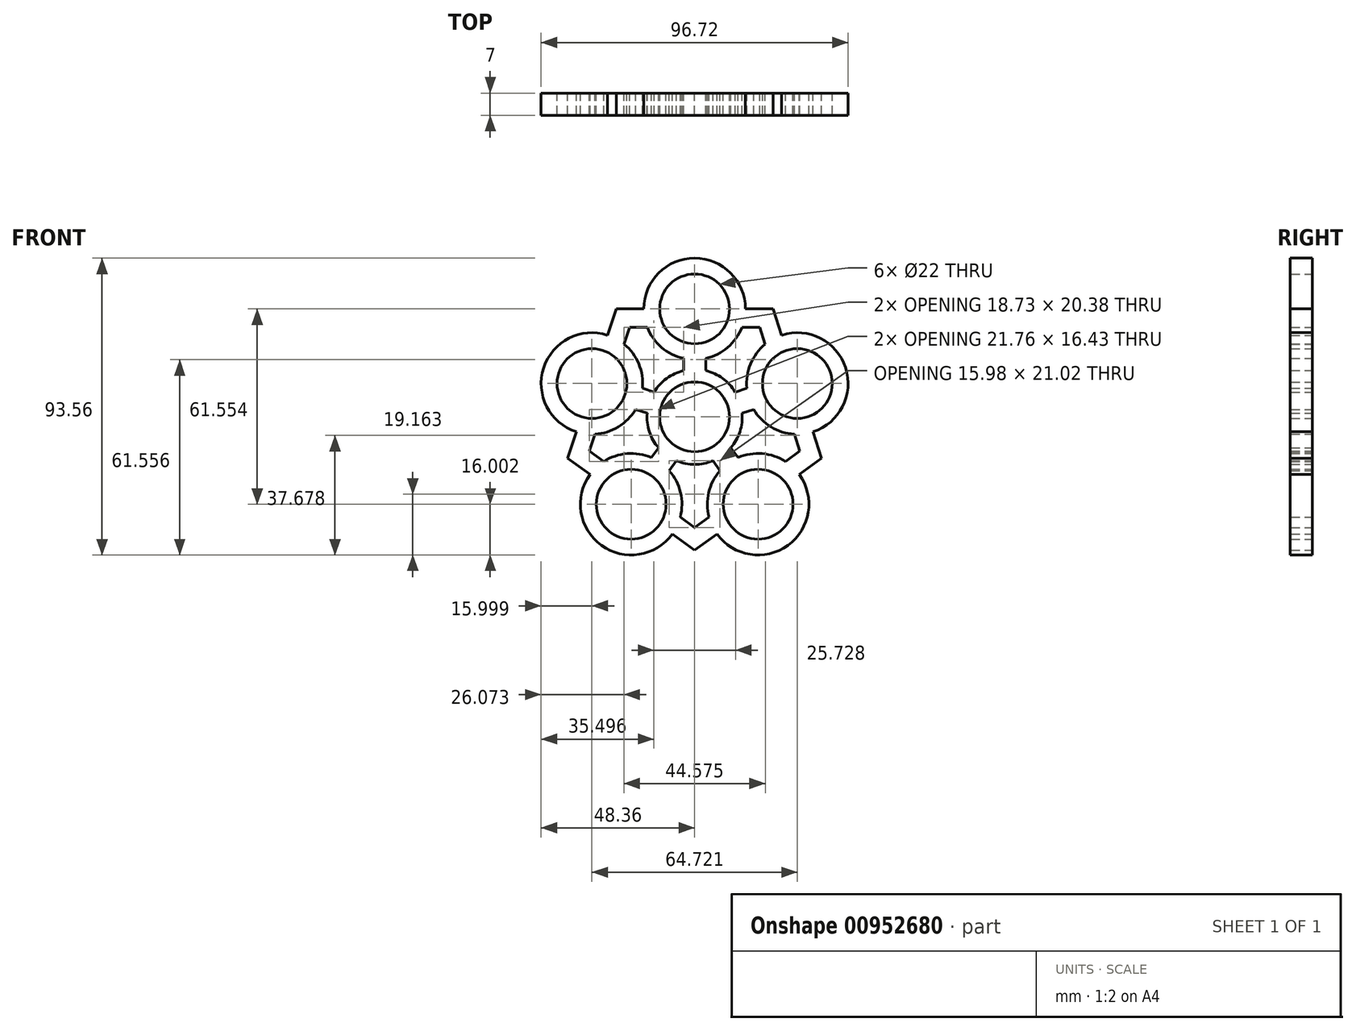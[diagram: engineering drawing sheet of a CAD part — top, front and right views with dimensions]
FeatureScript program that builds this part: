
annotation { "Feature Type Name" : "Feature", "Feature Type Description" : "" }
export const myFeature = defineFeature(function(context is Context, id is Id, definition is map)
    precondition{}
    {
        {
            var Q0;
            Q0=qCreatedBy(makeId("Front.planeOp"),FACE);
            var sketch = newSketch(context, id + "F0", { "sketchPlane" : qUnion([Q0])});
            skCircle(sketch, "E0", {"center": v(0, 0) * mm, "radius": 11 * mm});
            skCircle(sketch, "E1", {"center": v(0, 0) * mm, "radius": 15 * mm});
            skPoint(sketch, "E2.0.midPoint", {"position": v(0, -27.53) * mm});
            skCircle(sketch, "E3", {"center": v(0, 34.03) * mm, "radius": 11 * mm});
            skCircle(sketch, "E4", {"center": v(0, 34.03) * mm, "radius": 16 * mm});
            skCircle(sketch, "E5", {"center": v(32.36, 10.51) * mm, "radius": 11 * mm});
            skCircle(sketch, "E6", {"center": v(32.36, 10.51) * mm, "radius": 16 * mm});
            skCircle(sketch, "E7", {"center": v(20, -27.53) * mm, "radius": 11 * mm});
            skCircle(sketch, "E8", {"center": v(20, -27.53) * mm, "radius": 16 * mm});
            skCircle(sketch, "E9", {"center": v(-20, -27.53) * mm, "radius": 11 * mm});
            skCircle(sketch, "E10", {"center": v(-20, -27.53) * mm, "radius": 16 * mm});
            skCircle(sketch, "E11", {"center": v(-32.36, 10.51) * mm, "radius": 11 * mm});
            skCircle(sketch, "E12", {"center": v(-32.36, 10.51) * mm, "radius": 16 * mm});
            skPoint(sketch, "E13.0.midPoint", {"position": v(0, 28.22) * mm});
            skLineSegment(sketch, "E14.0", {"start": v(-24.72, 34.03) * mm, "end": v(-11, 34.03) * mm});
            skLineSegment(sketch, "E14.1", {"start": v(24.72, 34.03) * mm, "end": v(28.96, 20.98) * mm});
            skLineSegment(sketch, "E14.2", {"start": v(40, -13) * mm, "end": v(32.94, -18.12) * mm});
            skLineSegment(sketch, "E14.3", {"start": v(0, -42.06) * mm, "end": v(-11.1, -34) * mm});
            skLineSegment(sketch, "E14.4", {"start": v(-40, -13) * mm, "end": v(-35.76, 0.05) * mm});
            skLineSegment(sketch, "E15.trimOffspring", {"start": v(11, 34.03) * mm, "end": v(24.72, 34.03) * mm});
            skLineSegment(sketch, "E16.trimOffspring", {"start": v(7.06, -36.93) * mm, "end": v(0, -42.06) * mm});
            skLineSegment(sketch, "E17.trimOffspring", {"start": v(35.76, 0.05) * mm, "end": v(40, -13) * mm});
            skLineSegment(sketch, "E18.trimOffspring", {"start": v(-28.9, -21.06) * mm, "end": v(-40, -13) * mm});
            skLineSegment(sketch, "E19.trimOffspring", {"start": v(-28.96, 20.98) * mm, "end": v(-24.72, 34.03) * mm});
            skCircle(sketch, "E20.cCircle", {"center": v(0, 0) * mm, "radius": 28.22 * mm, "construction": true});
            skLineSegment(sketch, "E20.0", {"start": v(-20.5, 28.22) * mm, "end": v(20.5, 28.22) * mm});
            skLineSegment(sketch, "E20.1", {"start": v(20.5, 28.22) * mm, "end": v(33.17, -10.78) * mm});
            skLineSegment(sketch, "E20.2", {"start": v(33.17, -10.78) * mm, "end": v(0, -34.88) * mm});
            skLineSegment(sketch, "E20.3", {"start": v(0, -34.88) * mm, "end": v(-33.17, -10.78) * mm});
            skLineSegment(sketch, "E20.4", {"start": v(-33.17, -10.78) * mm, "end": v(-20.5, 28.22) * mm});
            skLineSegment(sketch, "E21", {"start": v(32.94, -18.12) * mm, "end": v(7.06, -36.93) * mm});
            skLineSegment(sketch, "E22", {"start": v(-11.1, -34) * mm, "end": v(-28.9, -21.06) * mm});
            skLineSegment(sketch, "E23", {"start": v(-35.76, 0.05) * mm, "end": v(-28.96, 20.98) * mm});
            skLineSegment(sketch, "E24", {"start": v(-11, 34.03) * mm, "end": v(11, 34.03) * mm});
            skLineSegment(sketch, "E25", {"start": v(28.96, 20.98) * mm, "end": v(35.76, 0.05) * mm});
            skCircle(sketch, "E26.cCircle", {"center": v(0, 0) * mm, "radius": 4.82 * mm, "construction": true});
            skLineSegment(sketch, "E26.0", {"start": v(-3.5, 4.82) * mm, "end": v(3.5, 4.82) * mm});
            skLineSegment(sketch, "E26.1", {"start": v(3.5, 4.82) * mm, "end": v(5.66, -1.84) * mm});
            skLineSegment(sketch, "E26.2", {"start": v(5.66, -1.84) * mm, "end": v(0, -5.95) * mm});
            skLineSegment(sketch, "E26.3", {"start": v(0, -5.95) * mm, "end": v(-5.66, -1.84) * mm});
            skLineSegment(sketch, "E26.4", {"start": v(-5.66, -1.84) * mm, "end": v(-3.5, 4.82) * mm});
            skPoint(sketch, "E26.0.midPoint", {"position": v(0, 4.82) * mm});
            skLineSegment(sketch, "E27", {"start": v(3.5, 4.82) * mm, "end": v(31.28, 13.84) * mm});
            skLineSegment(sketch, "E28", {"start": v(5.66, -1.84) * mm, "end": v(33.44, 7.19) * mm});
            skLineSegment(sketch, "E29", {"start": v(5.66, -1.84) * mm, "end": v(19.29, -20.6) * mm});
            skLineSegment(sketch, "E30", {"start": v(0, -5.95) * mm, "end": v(13.63, -24.7) * mm});
            skLineSegment(sketch, "E31", {"start": v(0, -5.95) * mm, "end": v(-13.63, -24.7) * mm});
            skLineSegment(sketch, "E32", {"start": v(-5.66, -1.84) * mm, "end": v(-19.29, -20.6) * mm});
            skLineSegment(sketch, "E33", {"start": v(-5.66, -1.84) * mm, "end": v(-27.7, 5.32) * mm});
            skLineSegment(sketch, "E34", {"start": v(-3.5, 4.82) * mm, "end": v(-25.55, 11.98) * mm});
            skLineSegment(sketch, "E35", {"start": v(-3.5, 4.82) * mm, "end": v(-3.5, 28) * mm});
            skLineSegment(sketch, "E36", {"start": v(3.5, 4.82) * mm, "end": v(3.5, 28) * mm});
            skSolve(sketch);
        }
        {
            var Q0;
            {var subQ1=sQuery(id+"F0.wireOp",EDGE,"E14.1");var subQ6=sQuery(id+"F0.wireOp",EDGE,"E6");var subQ8=makeQuery(id+"F0.imprint","INTERSECT",VERTEX,{"derivedFrom":[subQ6,subQ1]});Q0=makeQuery(id+"F0.imprint","IMPRINT",FACE,{"disambiguationData":[TD([[makeQuery(id+"F0.imprint","IMPRINT",EDGE,{"disambiguationData":[TD([[subQ8,1.0]])],"derivedFrom":subQ6}),1.0]])]});}
            var Q1;
            {var subQ0=sQuery(id+"F0.wireOp",EDGE,"E14.1");var subQ5=sQuery(id+"F0.wireOp",EDGE,"E6");var subQ6=makeQuery(id+"F0.imprint","INTERSECT",VERTEX,{"derivedFrom":[subQ5,subQ0]});Q1=makeQuery(id+"F0.imprint","IMPRINT",FACE,{"disambiguationData":[TD([[makeQuery(id+"F0.imprint","IMPRINT",EDGE,{"disambiguationData":[TD([[subQ6,-1.0]])],"derivedFrom":subQ5}),1.0]])]});}
            var Q2;
            {var subQ0=sQuery(id+"F0.wireOp",EDGE,"E20.1");var subQ1=sQuery(id+"F0.wireOp",EDGE,"E5");var subQ2=makeQuery(id+"F0.imprint","INTERSECT",VERTEX,{"disambiguationData":[OD(0.0)],"derivedFrom":[subQ1,subQ0]});Q2=makeQuery(id+"F0.imprint","IMPRINT",FACE,{"disambiguationData":[TD([[makeQuery(id+"F0.imprint","IMPRINT",EDGE,{"disambiguationData":[TD([[subQ2,-1.0]])],"derivedFrom":subQ1}),-1.0]])]});}
            var Q3;
            {var subQ0=sQuery(id+"F0.wireOp",EDGE,"E27");var subQ1=sQuery(id+"F0.wireOp",EDGE,"E5");var subQ2=makeQuery(id+"F0.imprint","INTERSECT",VERTEX,{"derivedFrom":[subQ1,subQ0]});Q3=makeQuery(id+"F0.imprint","IMPRINT",FACE,{"disambiguationData":[TD([[makeQuery(id+"F0.imprint","IMPRINT",EDGE,{"disambiguationData":[TD([[subQ2,-1.0]])],"derivedFrom":subQ1}),-1.0]])]});}
            var Q4;
            {var subQ0=sQuery(id+"F0.wireOp",EDGE,"E17.trimOffspring");var subQ5=sQuery(id+"F0.wireOp",EDGE,"E6");var subQ6=makeQuery(id+"F0.imprint","INTERSECT",VERTEX,{"derivedFrom":[subQ5,subQ0]});Q4=makeQuery(id+"F0.imprint","IMPRINT",FACE,{"disambiguationData":[TD([[makeQuery(id+"F0.imprint","IMPRINT",EDGE,{"disambiguationData":[TD([[subQ6,1.0]])],"derivedFrom":subQ5}),1.0]])]});}
            var Q5;
            {var subQ0=sQuery(id+"F0.wireOp",EDGE,"E28");var subQ1=sQuery(id+"F0.wireOp",EDGE,"E5");var subQ2=makeQuery(id+"F0.imprint","INTERSECT",VERTEX,{"derivedFrom":[subQ1,subQ0]});Q5=makeQuery(id+"F0.imprint","IMPRINT",FACE,{"disambiguationData":[TD([[makeQuery(id+"F0.imprint","IMPRINT",EDGE,{"disambiguationData":[TD([[subQ2,-1.0]])],"derivedFrom":subQ1}),-1.0]])]});}
            var Q6;
            {var subQ1=sQuery(id+"F0.wireOp",EDGE,"E14.2");Q6=makeQuery(id+"F0.imprint","IMPRINT",FACE,{"disambiguationData":[TD([[makeQuery(id+"F0.imprint","IMPRINT",EDGE,{"derivedFrom":subQ1}),-1.0]])]});}
            var Q7;
            {var subQ0=sQuery(id+"F0.wireOp",EDGE,"E21");var subQ1=sQuery(id+"F0.wireOp",EDGE,"E7");var subQ2=makeQuery(id+"F0.imprint","INTERSECT",VERTEX,{"disambiguationData":[OD(0.0)],"derivedFrom":[subQ1,subQ0]});Q7=makeQuery(id+"F0.imprint","IMPRINT",FACE,{"disambiguationData":[TD([[makeQuery(id+"F0.imprint","IMPRINT",EDGE,{"disambiguationData":[TD([[subQ2,1.0]])],"derivedFrom":subQ1}),-1.0]])]});}
            var Q8;
            {var subQ0=sQuery(id+"F0.wireOp",EDGE,"E20.2");var subQ1=sQuery(id+"F0.wireOp",EDGE,"E7");var subQ2=makeQuery(id+"F0.imprint","INTERSECT",VERTEX,{"disambiguationData":[OD(0.0)],"derivedFrom":[subQ1,subQ0]});Q8=makeQuery(id+"F0.imprint","IMPRINT",FACE,{"disambiguationData":[TD([[makeQuery(id+"F0.imprint","IMPRINT",EDGE,{"disambiguationData":[TD([[subQ2,1.0]])],"derivedFrom":subQ1}),-1.0]])]});}
            var Q9;
            {var subQ0=sQuery(id+"F0.wireOp",EDGE,"E29");var subQ1=sQuery(id+"F0.wireOp",EDGE,"E7");var subQ2=makeQuery(id+"F0.imprint","INTERSECT",VERTEX,{"derivedFrom":[subQ1,subQ0]});Q9=makeQuery(id+"F0.imprint","IMPRINT",FACE,{"disambiguationData":[TD([[makeQuery(id+"F0.imprint","IMPRINT",EDGE,{"disambiguationData":[TD([[subQ2,1.0]])],"derivedFrom":subQ1}),-1.0]])]});}
            var Q10;
            {var subQ0=sQuery(id+"F0.wireOp",EDGE,"E29");var subQ1=sQuery(id+"F0.wireOp",EDGE,"E7");var subQ2=makeQuery(id+"F0.imprint","INTERSECT",VERTEX,{"derivedFrom":[subQ1,subQ0]});Q10=makeQuery(id+"F0.imprint","IMPRINT",FACE,{"disambiguationData":[TD([[makeQuery(id+"F0.imprint","IMPRINT",EDGE,{"disambiguationData":[TD([[subQ2,-1.0]])],"derivedFrom":subQ1}),-1.0]])]});}
            var Q11;
            {var subQ0=sQuery(id+"F0.wireOp",EDGE,"E30");var subQ1=sQuery(id+"F0.wireOp",EDGE,"E7");var subQ2=makeQuery(id+"F0.imprint","INTERSECT",VERTEX,{"derivedFrom":[subQ1,subQ0]});Q11=makeQuery(id+"F0.imprint","IMPRINT",FACE,{"disambiguationData":[TD([[makeQuery(id+"F0.imprint","IMPRINT",EDGE,{"disambiguationData":[TD([[subQ2,-1.0]])],"derivedFrom":subQ1}),-1.0]])]});}
            var Q12;
            {var subQ0=sQuery(id+"F0.wireOp",EDGE,"E20.2");var subQ1=sQuery(id+"F0.wireOp",EDGE,"E7");var subQ2=makeQuery(id+"F0.imprint","INTERSECT",VERTEX,{"disambiguationData":[OD(1.0)],"derivedFrom":[subQ1,subQ0]});Q12=makeQuery(id+"F0.imprint","IMPRINT",FACE,{"disambiguationData":[TD([[makeQuery(id+"F0.imprint","IMPRINT",EDGE,{"disambiguationData":[TD([[subQ2,-1.0]])],"derivedFrom":subQ1}),-1.0]])]});}
            var Q13;
            {var subQ0=sQuery(id+"F0.wireOp",EDGE,"E14.3");var subQ5=sQuery(id+"F0.wireOp",EDGE,"E10");var subQ6=makeQuery(id+"F0.imprint","INTERSECT",VERTEX,{"derivedFrom":[subQ5,subQ0]});Q13=makeQuery(id+"F0.imprint","IMPRINT",FACE,{"disambiguationData":[TD([[makeQuery(id+"F0.imprint","IMPRINT",EDGE,{"disambiguationData":[TD([[subQ6,-1.0]])],"derivedFrom":subQ5}),1.0]])]});}
            var Q14;
            {var subQ4=sQuery(id+"F0.wireOp",EDGE,"E18.trimOffspring");var subQ6=sQuery(id+"F0.wireOp",EDGE,"E10");var subQ7=makeQuery(id+"F0.imprint","INTERSECT",VERTEX,{"derivedFrom":[subQ6,subQ4]});Q14=makeQuery(id+"F0.imprint","IMPRINT",FACE,{"disambiguationData":[TD([[makeQuery(id+"F0.imprint","IMPRINT",EDGE,{"disambiguationData":[TD([[subQ7,-1.0]])],"derivedFrom":subQ6}),1.0]])]});}
            var Q15;
            {var subQ0=sQuery(id+"F0.wireOp",EDGE,"E31");var subQ1=sQuery(id+"F0.wireOp",EDGE,"E9");var subQ2=makeQuery(id+"F0.imprint","INTERSECT",VERTEX,{"derivedFrom":[subQ1,subQ0]});Q15=makeQuery(id+"F0.imprint","IMPRINT",FACE,{"disambiguationData":[TD([[makeQuery(id+"F0.imprint","IMPRINT",EDGE,{"disambiguationData":[TD([[subQ2,1.0]])],"derivedFrom":subQ1}),-1.0]])]});}
            var Q16;
            {var subQ0=sQuery(id+"F0.wireOp",EDGE,"E32");var subQ1=sQuery(id+"F0.wireOp",EDGE,"E9");var subQ2=makeQuery(id+"F0.imprint","INTERSECT",VERTEX,{"derivedFrom":[subQ1,subQ0]});Q16=makeQuery(id+"F0.imprint","IMPRINT",FACE,{"disambiguationData":[TD([[makeQuery(id+"F0.imprint","IMPRINT",EDGE,{"disambiguationData":[TD([[subQ2,1.0]])],"derivedFrom":subQ1}),-1.0]])]});}
            var Q17;
            {var subQ0=sQuery(id+"F0.wireOp",EDGE,"E32");var subQ1=sQuery(id+"F0.wireOp",EDGE,"E9");var subQ2=makeQuery(id+"F0.imprint","INTERSECT",VERTEX,{"derivedFrom":[subQ1,subQ0]});Q17=makeQuery(id+"F0.imprint","IMPRINT",FACE,{"disambiguationData":[TD([[makeQuery(id+"F0.imprint","IMPRINT",EDGE,{"disambiguationData":[TD([[subQ2,-1.0]])],"derivedFrom":subQ1}),-1.0]])]});}
            var Q18;
            {var subQ0=sQuery(id+"F0.wireOp",EDGE,"E18.trimOffspring");var subQ5=sQuery(id+"F0.wireOp",EDGE,"E10");var subQ7=makeQuery(id+"F0.imprint","INTERSECT",VERTEX,{"derivedFrom":[subQ5,subQ0]});Q18=makeQuery(id+"F0.imprint","IMPRINT",FACE,{"disambiguationData":[TD([[makeQuery(id+"F0.imprint","IMPRINT",EDGE,{"disambiguationData":[TD([[subQ7,1.0]])],"derivedFrom":subQ5}),1.0]])]});}
            var Q19;
            {var subQ0=sQuery(id+"F0.wireOp",EDGE,"E14.4");var subQ5=sQuery(id+"F0.wireOp",EDGE,"E12");var subQ6=makeQuery(id+"F0.imprint","INTERSECT",VERTEX,{"derivedFrom":[subQ5,subQ0]});Q19=makeQuery(id+"F0.imprint","IMPRINT",FACE,{"disambiguationData":[TD([[makeQuery(id+"F0.imprint","IMPRINT",EDGE,{"disambiguationData":[TD([[subQ6,-1.0]])],"derivedFrom":subQ5}),1.0]])]});}
            var Q20;
            {var subQ0=sQuery(id+"F0.wireOp",EDGE,"E33");var subQ1=sQuery(id+"F0.wireOp",EDGE,"E11");var subQ2=makeQuery(id+"F0.imprint","INTERSECT",VERTEX,{"derivedFrom":[subQ1,subQ0]});Q20=makeQuery(id+"F0.imprint","IMPRINT",FACE,{"disambiguationData":[TD([[makeQuery(id+"F0.imprint","IMPRINT",EDGE,{"disambiguationData":[TD([[subQ2,1.0]])],"derivedFrom":subQ1}),-1.0]])]});}
            var Q21;
            {var subQ0=sQuery(id+"F0.wireOp",EDGE,"E34");var subQ1=sQuery(id+"F0.wireOp",EDGE,"E11");var subQ2=makeQuery(id+"F0.imprint","INTERSECT",VERTEX,{"derivedFrom":[subQ1,subQ0]});Q21=makeQuery(id+"F0.imprint","IMPRINT",FACE,{"disambiguationData":[TD([[makeQuery(id+"F0.imprint","IMPRINT",EDGE,{"disambiguationData":[TD([[subQ2,-1.0]])],"derivedFrom":subQ1}),-1.0]])]});}
            var Q22;
            {var subQ0=sQuery(id+"F0.wireOp",EDGE,"E19.trimOffspring");var subQ5=sQuery(id+"F0.wireOp",EDGE,"E12");var subQ6=makeQuery(id+"F0.imprint","INTERSECT",VERTEX,{"derivedFrom":[subQ5,subQ0]});Q22=makeQuery(id+"F0.imprint","IMPRINT",FACE,{"disambiguationData":[TD([[makeQuery(id+"F0.imprint","IMPRINT",EDGE,{"disambiguationData":[TD([[subQ6,1.0]])],"derivedFrom":subQ5}),1.0]])]});}
            var Q23;
            {var subQ4=sQuery(id+"F0.wireOp",EDGE,"E19.trimOffspring");var subQ6=sQuery(id+"F0.wireOp",EDGE,"E12");var subQ7=makeQuery(id+"F0.imprint","INTERSECT",VERTEX,{"derivedFrom":[subQ6,subQ4]});Q23=makeQuery(id+"F0.imprint","IMPRINT",FACE,{"disambiguationData":[TD([[makeQuery(id+"F0.imprint","IMPRINT",EDGE,{"disambiguationData":[TD([[subQ7,-1.0]])],"derivedFrom":subQ6}),1.0]])]});}
            var Q24;
            {var subQ1=sQuery(id+"F0.wireOp",EDGE,"E14.0");var subQ6=sQuery(id+"F0.wireOp",EDGE,"E4");var subQ7=makeQuery(id+"F0.imprint","INTERSECT",VERTEX,{"derivedFrom":[subQ6,subQ1]});Q24=makeQuery(id+"F0.imprint","IMPRINT",FACE,{"disambiguationData":[TD([[makeQuery(id+"F0.imprint","IMPRINT",EDGE,{"disambiguationData":[TD([[subQ7,1.0]])],"derivedFrom":subQ6}),1.0]])]});}
            var Q25;
            {var subQ0=sQuery(id+"F0.wireOp",EDGE,"E15.trimOffspring");var subQ5=sQuery(id+"F0.wireOp",EDGE,"E4");var subQ6=makeQuery(id+"F0.imprint","INTERSECT",VERTEX,{"derivedFrom":[subQ5,subQ0]});Q25=makeQuery(id+"F0.imprint","IMPRINT",FACE,{"disambiguationData":[TD([[makeQuery(id+"F0.imprint","IMPRINT",EDGE,{"disambiguationData":[TD([[subQ6,1.0]])],"derivedFrom":subQ5}),1.0]])]});}
            var Q26;
            {var subQ0=sQuery(id+"F0.wireOp",EDGE,"E36");var subQ1=sQuery(id+"F0.wireOp",EDGE,"E3");var subQ2=makeQuery(id+"F0.imprint","INTERSECT",VERTEX,{"derivedFrom":[subQ1,subQ0]});Q26=makeQuery(id+"F0.imprint","IMPRINT",FACE,{"disambiguationData":[TD([[makeQuery(id+"F0.imprint","IMPRINT",EDGE,{"disambiguationData":[TD([[subQ2,-1.0]])],"derivedFrom":subQ1}),-1.0]])]});}
            var Q27;
            {var subQ0=sQuery(id+"F0.wireOp",EDGE,"E35");var subQ1=sQuery(id+"F0.wireOp",EDGE,"E3");var subQ2=makeQuery(id+"F0.imprint","INTERSECT",VERTEX,{"derivedFrom":[subQ1,subQ0]});Q27=makeQuery(id+"F0.imprint","IMPRINT",FACE,{"disambiguationData":[TD([[makeQuery(id+"F0.imprint","IMPRINT",EDGE,{"disambiguationData":[TD([[subQ2,1.0]])],"derivedFrom":subQ1}),-1.0]])]});}
            var Q28;
            {var subQ0=sQuery(id+"F0.wireOp",EDGE,"E14.0");var subQ5=sQuery(id+"F0.wireOp",EDGE,"E4");var subQ6=makeQuery(id+"F0.imprint","INTERSECT",VERTEX,{"derivedFrom":[subQ5,subQ0]});Q28=makeQuery(id+"F0.imprint","IMPRINT",FACE,{"disambiguationData":[TD([[makeQuery(id+"F0.imprint","IMPRINT",EDGE,{"disambiguationData":[TD([[subQ6,-1.0]])],"derivedFrom":subQ5}),1.0]])]});}
            var Q29;
            {var subQ0=sQuery(id+"F0.wireOp",EDGE,"E35");var subQ1=sQuery(id+"F0.wireOp",EDGE,"E3");var subQ2=makeQuery(id+"F0.imprint","INTERSECT",VERTEX,{"derivedFrom":[subQ1,subQ0]});Q29=makeQuery(id+"F0.imprint","IMPRINT",FACE,{"disambiguationData":[TD([[makeQuery(id+"F0.imprint","IMPRINT",EDGE,{"disambiguationData":[TD([[subQ2,-1.0]])],"derivedFrom":subQ1}),-1.0]])]});}
            var Q30;
            {var subQ0=sQuery(id+"F0.wireOp",EDGE,"E34");var subQ1=sQuery(id+"F0.wireOp",EDGE,"E11");var subQ2=makeQuery(id+"F0.imprint","INTERSECT",VERTEX,{"derivedFrom":[subQ1,subQ0]});Q30=makeQuery(id+"F0.imprint","IMPRINT",FACE,{"disambiguationData":[TD([[makeQuery(id+"F0.imprint","IMPRINT",EDGE,{"disambiguationData":[TD([[subQ2,1.0]])],"derivedFrom":subQ1}),-1.0]])]});}
            var Q31;
            {var subQ0=sQuery(id+"F0.wireOp",EDGE,"E34");var subQ1=sQuery(id+"F0.wireOp",EDGE,"E1");var subQ2=makeQuery(id+"F0.imprint","INTERSECT",VERTEX,{"derivedFrom":[subQ1,subQ0]});Q31=makeQuery(id+"F0.imprint","IMPRINT",FACE,{"disambiguationData":[TD([[makeQuery(id+"F0.imprint","IMPRINT",EDGE,{"disambiguationData":[TD([[subQ2,-1.0]])],"derivedFrom":subQ1}),-1.0]])]});}
            var Q32;
            {var subQ0=sQuery(id+"F0.wireOp",EDGE,"E34");var subQ1=sQuery(id+"F0.wireOp",EDGE,"E0");var subQ2=makeQuery(id+"F0.imprint","INTERSECT",VERTEX,{"derivedFrom":[subQ1,subQ0]});Q32=makeQuery(id+"F0.imprint","IMPRINT",FACE,{"disambiguationData":[TD([[makeQuery(id+"F0.imprint","IMPRINT",EDGE,{"disambiguationData":[TD([[subQ2,-1.0]])],"derivedFrom":subQ1}),-1.0]])]});}
            var Q33;
            {var subQ0=sQuery(id+"F0.wireOp",EDGE,"E33");var subQ1=sQuery(id+"F0.wireOp",EDGE,"E0");var subQ2=makeQuery(id+"F0.imprint","INTERSECT",VERTEX,{"derivedFrom":[subQ1,subQ0]});Q33=makeQuery(id+"F0.imprint","IMPRINT",FACE,{"disambiguationData":[TD([[makeQuery(id+"F0.imprint","IMPRINT",EDGE,{"disambiguationData":[TD([[subQ2,-1.0]])],"derivedFrom":subQ1}),-1.0]])]});}
            var Q34;
            {var subQ0=sQuery(id+"F0.wireOp",EDGE,"E32");var subQ1=sQuery(id+"F0.wireOp",EDGE,"E0");var subQ2=makeQuery(id+"F0.imprint","INTERSECT",VERTEX,{"derivedFrom":[subQ1,subQ0]});Q34=makeQuery(id+"F0.imprint","IMPRINT",FACE,{"disambiguationData":[TD([[makeQuery(id+"F0.imprint","IMPRINT",EDGE,{"disambiguationData":[TD([[subQ2,-1.0]])],"derivedFrom":subQ1}),-1.0]])]});}
            var Q35;
            {var subQ0=sQuery(id+"F0.wireOp",EDGE,"E32");var subQ1=sQuery(id+"F0.wireOp",EDGE,"E1");var subQ2=makeQuery(id+"F0.imprint","INTERSECT",VERTEX,{"derivedFrom":[subQ1,subQ0]});Q35=makeQuery(id+"F0.imprint","IMPRINT",FACE,{"disambiguationData":[TD([[makeQuery(id+"F0.imprint","IMPRINT",EDGE,{"disambiguationData":[TD([[subQ2,-1.0]])],"derivedFrom":subQ1}),-1.0]])]});}
            var Q36;
            {var subQ0=sQuery(id+"F0.wireOp",EDGE,"E30");var subQ1=sQuery(id+"F0.wireOp",EDGE,"E0");var subQ2=makeQuery(id+"F0.imprint","INTERSECT",VERTEX,{"derivedFrom":[subQ1,subQ0]});Q36=makeQuery(id+"F0.imprint","IMPRINT",FACE,{"disambiguationData":[TD([[makeQuery(id+"F0.imprint","IMPRINT",EDGE,{"disambiguationData":[TD([[subQ2,-1.0]])],"derivedFrom":subQ1}),-1.0]])]});}
            var Q37;
            {var subQ0=sQuery(id+"F0.wireOp",EDGE,"E31");var subQ1=sQuery(id+"F0.wireOp",EDGE,"E0");var subQ2=makeQuery(id+"F0.imprint","INTERSECT",VERTEX,{"derivedFrom":[subQ1,subQ0]});Q37=makeQuery(id+"F0.imprint","IMPRINT",FACE,{"disambiguationData":[TD([[makeQuery(id+"F0.imprint","IMPRINT",EDGE,{"disambiguationData":[TD([[subQ2,-1.0]])],"derivedFrom":subQ1}),-1.0]])]});}
            var Q38;
            {var subQ0=sQuery(id+"F0.wireOp",EDGE,"E27");var subQ1=sQuery(id+"F0.wireOp",EDGE,"E0");var subQ2=makeQuery(id+"F0.imprint","INTERSECT",VERTEX,{"derivedFrom":[subQ1,subQ0]});Q38=makeQuery(id+"F0.imprint","IMPRINT",FACE,{"disambiguationData":[TD([[makeQuery(id+"F0.imprint","IMPRINT",EDGE,{"disambiguationData":[TD([[subQ2,1.0]])],"derivedFrom":subQ1}),-1.0]])]});}
            var Q39;
            {var subQ0=sQuery(id+"F0.wireOp",EDGE,"E27");var subQ1=sQuery(id+"F0.wireOp",EDGE,"E1");var subQ2=makeQuery(id+"F0.imprint","INTERSECT",VERTEX,{"derivedFrom":[subQ1,subQ0]});Q39=makeQuery(id+"F0.imprint","IMPRINT",FACE,{"disambiguationData":[TD([[makeQuery(id+"F0.imprint","IMPRINT",EDGE,{"disambiguationData":[TD([[subQ2,1.0]])],"derivedFrom":subQ1}),-1.0]])]});}
            var Q40;
            {var subQ0=sQuery(id+"F0.wireOp",EDGE,"E36");var subQ1=sQuery(id+"F0.wireOp",EDGE,"E0");var subQ2=makeQuery(id+"F0.imprint","INTERSECT",VERTEX,{"derivedFrom":[subQ1,subQ0]});Q40=makeQuery(id+"F0.imprint","IMPRINT",FACE,{"disambiguationData":[TD([[makeQuery(id+"F0.imprint","IMPRINT",EDGE,{"disambiguationData":[TD([[subQ2,1.0]])],"derivedFrom":subQ1}),-1.0]])]});}
            var Q41;
            {var subQ0=sQuery(id+"F0.wireOp",EDGE,"E36");var subQ1=sQuery(id+"F0.wireOp",EDGE,"E0");var subQ2=makeQuery(id+"F0.imprint","INTERSECT",VERTEX,{"derivedFrom":[subQ1,subQ0]});Q41=makeQuery(id+"F0.imprint","IMPRINT",FACE,{"disambiguationData":[TD([[makeQuery(id+"F0.imprint","IMPRINT",EDGE,{"disambiguationData":[TD([[subQ2,-1.0]])],"derivedFrom":subQ1}),-1.0]])]});}
            var Q42;
            {var subQ0=sQuery(id+"F0.wireOp",EDGE,"E36");var subQ1=sQuery(id+"F0.wireOp",EDGE,"E1");var subQ2=makeQuery(id+"F0.imprint","INTERSECT",VERTEX,{"derivedFrom":[subQ1,subQ0]});Q42=makeQuery(id+"F0.imprint","IMPRINT",FACE,{"disambiguationData":[TD([[makeQuery(id+"F0.imprint","IMPRINT",EDGE,{"disambiguationData":[TD([[subQ2,-1.0]])],"derivedFrom":subQ1}),-1.0]])]});}
            var Q43;
            {var subQ0=sQuery(id+"F0.wireOp",EDGE,"E35");var subQ1=sQuery(id+"F0.wireOp",EDGE,"E0");var subQ2=makeQuery(id+"F0.imprint","INTERSECT",VERTEX,{"derivedFrom":[subQ1,subQ0]});Q43=makeQuery(id+"F0.imprint","IMPRINT",FACE,{"disambiguationData":[TD([[makeQuery(id+"F0.imprint","IMPRINT",EDGE,{"disambiguationData":[TD([[subQ2,-1.0]])],"derivedFrom":subQ1}),-1.0]])]});}
            var Q44;
            {var subQ0=sQuery(id+"F0.wireOp",EDGE,"E29");var subQ1=sQuery(id+"F0.wireOp",EDGE,"E0");var subQ2=makeQuery(id+"F0.imprint","INTERSECT",VERTEX,{"derivedFrom":[subQ1,subQ0]});Q44=makeQuery(id+"F0.imprint","IMPRINT",FACE,{"disambiguationData":[TD([[makeQuery(id+"F0.imprint","IMPRINT",EDGE,{"disambiguationData":[TD([[subQ2,-1.0]])],"derivedFrom":subQ1}),-1.0]])]});}
            var Q45;
            {var subQ0=sQuery(id+"F0.wireOp",EDGE,"E15.trimOffspring");var subQ3=sQuery(id+"F0.wireOp",EDGE,"E4");var subQ4=makeQuery(id+"F0.imprint","INTERSECT",VERTEX,{"derivedFrom":[subQ3,subQ0]});Q45=makeQuery(id+"F0.imprint","IMPRINT",FACE,{"disambiguationData":[TD([[makeQuery(id+"F0.imprint","IMPRINT",EDGE,{"disambiguationData":[TD([[subQ4,1.0]])],"derivedFrom":subQ3}),-1.0]])]});}
            var Q46;
            {var subQ1=sQuery(id+"F0.wireOp",EDGE,"E14.0");var subQ3=sQuery(id+"F0.wireOp",EDGE,"E4");var subQ4=makeQuery(id+"F0.imprint","INTERSECT",VERTEX,{"derivedFrom":[subQ3,subQ1]});Q46=makeQuery(id+"F0.imprint","IMPRINT",FACE,{"disambiguationData":[TD([[makeQuery(id+"F0.imprint","IMPRINT",EDGE,{"disambiguationData":[TD([[subQ4,-1.0]])],"derivedFrom":subQ3}),-1.0]])]});}
            var Q47;
            {var subQ0=sQuery(id+"F0.wireOp",EDGE,"E16.trimOffspring");Q47=makeQuery(id+"F0.imprint","IMPRINT",FACE,{"disambiguationData":[TD([[makeQuery(id+"F0.imprint","IMPRINT",EDGE,{"derivedFrom":subQ0}),-1.0]])]});}
            var Q48;
            {var subQ0=sQuery(id+"F0.wireOp",EDGE,"E18.trimOffspring");var subQ3=sQuery(id+"F0.wireOp",EDGE,"E10");var subQ4=makeQuery(id+"F0.imprint","INTERSECT",VERTEX,{"derivedFrom":[subQ3,subQ0]});Q48=makeQuery(id+"F0.imprint","IMPRINT",FACE,{"disambiguationData":[TD([[makeQuery(id+"F0.imprint","IMPRINT",EDGE,{"disambiguationData":[TD([[subQ4,1.0]])],"derivedFrom":subQ3}),-1.0]])]});}
            var Q49;
            {var subQ0=sQuery(id+"F0.wireOp",EDGE,"E30");var subQ1=sQuery(id+"F0.wireOp",EDGE,"E1");var subQ2=makeQuery(id+"F0.imprint","INTERSECT",VERTEX,{"derivedFrom":[subQ1,subQ0]});Q49=makeQuery(id+"F0.imprint","IMPRINT",FACE,{"disambiguationData":[TD([[makeQuery(id+"F0.imprint","IMPRINT",EDGE,{"disambiguationData":[TD([[subQ2,-1.0]])],"derivedFrom":subQ1}),-1.0]])]});}
            extrude(context, id + "F1", {"entities" : qUnion([Q0, Q1, Q2, Q3, Q4, Q5, Q6, Q7, Q8, Q9, Q10, Q11, Q12, Q13, Q14, Q15, Q16, Q17, Q18, Q19, Q20, Q21, Q22, Q23, Q24, Q25, Q26, Q27, Q28, Q29, Q30, Q31, Q32, Q33, Q34, Q35, Q36, Q37, Q38, Q39, Q40, Q41, Q42, Q43, Q44, Q45, Q46, Q47, Q48, Q49]), "depth" : 7 * mm, "offsetDistance" : 25 * mm});
        }
    });
